# Revit family: Haworth_Planes_ConferenceTable_Polygon
name_source: partatom
category: Furniture Systems
revit_build: Autodesk Revit 2018 (Build: 20170223_1515(x64)
units: mm (PartAtom-declared; Revit-internal decimal feet)

## family parameters
Always vertical = Yes
Cut with Voids When Loaded = No
OmniClass Number = 23.40.70.14.64.21
OmniClass Title = Systems Furniture
Part Type = Normal
Room Calculation Point = No
Round Connector Dimension = Use Diameter
Shared = No
Work Plane-Based = No

## types (2) — shared parameters
Actual Height = 29"
Assembly Code = E2020200
Cutout = No
Cutout Depth = 4"
Cutout Width = 8"
Description = Haworth - Planes - Conference Table - Polygon
Flip Top = No
Leg Finish = Haworth _ Paint _ Metallic Champagne
Leg Height = 27 13/16"
Manufacturer = Haworth
Max. Depth = 43 115/128"
Max. Width = 77 51/128"
Min. Depth = 36 1/2"
Min. Width = 66"
Min/Max Depth = 30 or 36 in.
Min/Max Width = 60 or 72 in.
Model = Haworth - Planes - Conference Table - Polygon
Opening Double = No
Opening Double Wide = No
Opening Single = No
Opening Single Wide = No
Revision Number = 3
Size = Verify Final Dim. w/ Haworth
Support Spacing - From Edge = 13"
Support Spacing Outside - From Edge = 8"
Sustainability Info = http://www.haworth.com
Table Edge Finish = Haworth _ Laminate _ Maple H-AE
Table Finish = Haworth _ Laminate _ Maple H-AE
Table Thickness = 1 3/16"
URL = www.haworth.com
URL - Product = http://www.haworth.com
Warranty = http://www.haworth.com

## per-type parameters (varying)
| type | Actual Depth | Actual Width | Large |
| Standard | 36 1/2" | 66" | No |
| Large | 43 115/128" | 77 51/128" | Yes |

## geometry (parser evidence)
native form markers: Sweep x10
no freeform markers — native parametric forms only
